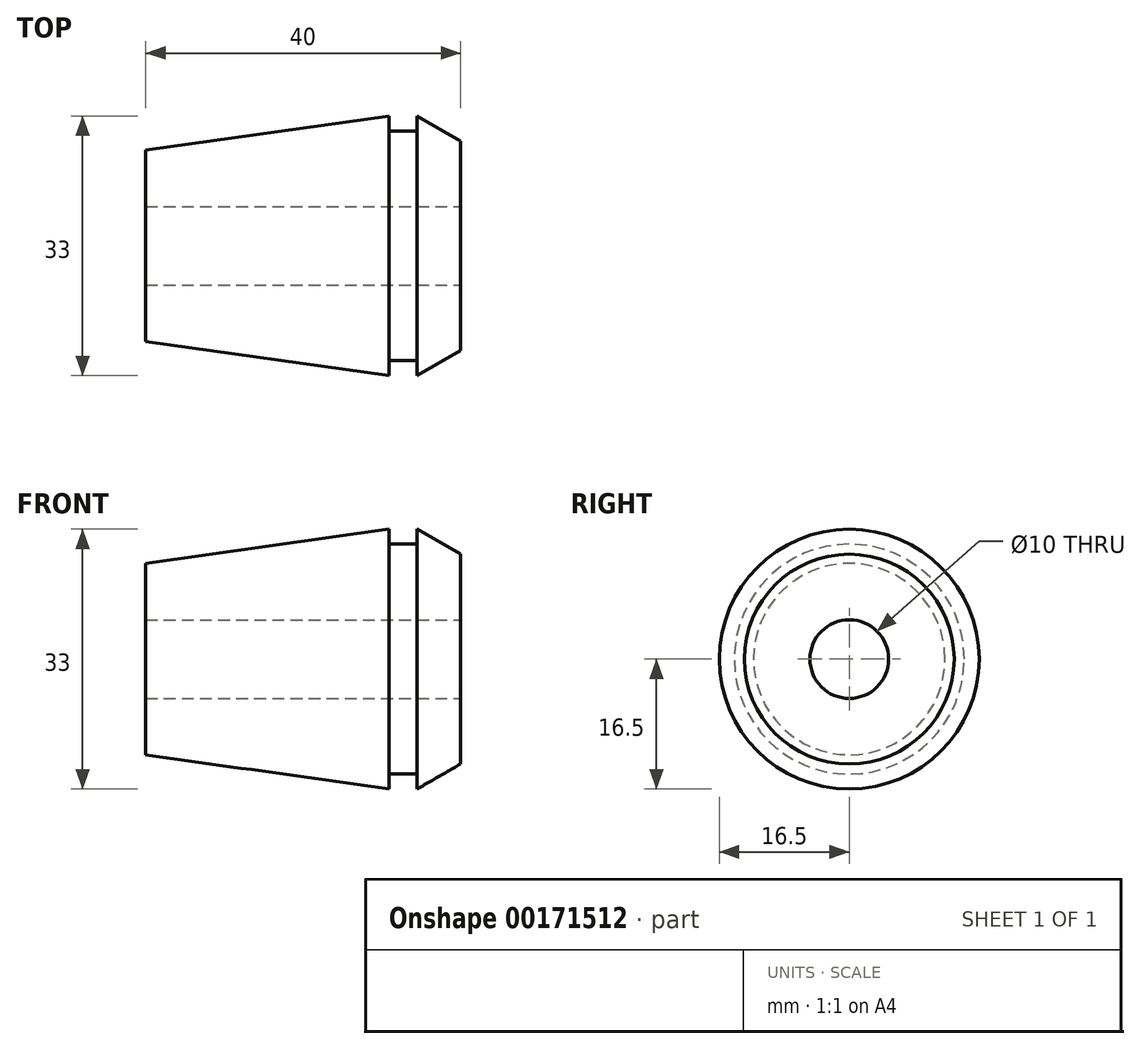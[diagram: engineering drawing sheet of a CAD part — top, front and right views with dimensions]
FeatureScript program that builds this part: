
annotation { "Feature Type Name" : "Feature", "Feature Type Description" : "" }
export const myFeature = defineFeature(function(context is Context, id is Id, definition is map)
    precondition{}
    {
        {
            var Q0;
            Q0=qCreatedBy(makeId("Front.planeOp"),FACE);
            var sketch = newSketch(context, id + "F0", { "sketchPlane" : qUnion([Q0])});
            skLineSegment(sketch, "E0", {"start": v(0, 0) * mm, "end": v(-24.63, 0) * mm, "construction": true});
            skLineSegment(sketch, "E1", {"start": v(0, 5) * mm, "end": v(0, 13.32) * mm});
            skLineSegment(sketch, "E2", {"start": v(0, 13.32) * mm, "end": v(-5.5, 16.5) * mm});
            skLineSegment(sketch, "E3", {"start": v(-5.5, 16.5) * mm, "end": v(-5.5, 14.6) * mm});
            skLineSegment(sketch, "E4", {"start": v(-5.5, 14.6) * mm, "end": v(-9.1, 14.6) * mm});
            skLineSegment(sketch, "E5", {"start": v(-9.1, 14.6) * mm, "end": v(-9.1, 16.5) * mm});
            skLineSegment(sketch, "E6", {"start": v(-9.1, 16.5) * mm, "end": v(-40, 12.16) * mm});
            skLineSegment(sketch, "E7", {"start": v(-40, 12.16) * mm, "end": v(-40, 5) * mm});
            skLineSegment(sketch, "E8", {"start": v(-40, 5) * mm, "end": v(0, 5) * mm});
            skLineSegment(sketch, "E9", {"start": v(-5.5, 16.5) * mm, "end": v(3.9, 16.5) * mm, "construction": true});
            skPoint(sketch, "E10", {"position": v(-12.66, 16) * mm});
            skLineSegment(sketch, "E11", {"start": v(-12.66, 16) * mm, "end": v(-31.9, 16) * mm, "construction": true});
            skSolve(sketch);
        }
        {
            var Q0;
            Q0=makeQuery(id+"F0.imprint","IMPRINT",FACE,{"disambiguationData":[TD([[makeQuery(id+"F0.imprint","IMPRINT",EDGE,{"derivedFrom":sQuery(id+"F0.wireOp",EDGE,"E1")}),1.0]])]});
            var Q1;
            Q1=sQuery(id+"F0.wireOp",EDGE,"E0");
            revolve(context, id + "F1", {"entities" : qUnion([Q0]), "axis" : qUnion([Q1]), "revolveType" : RevolveType.FULL});
        }
    });
